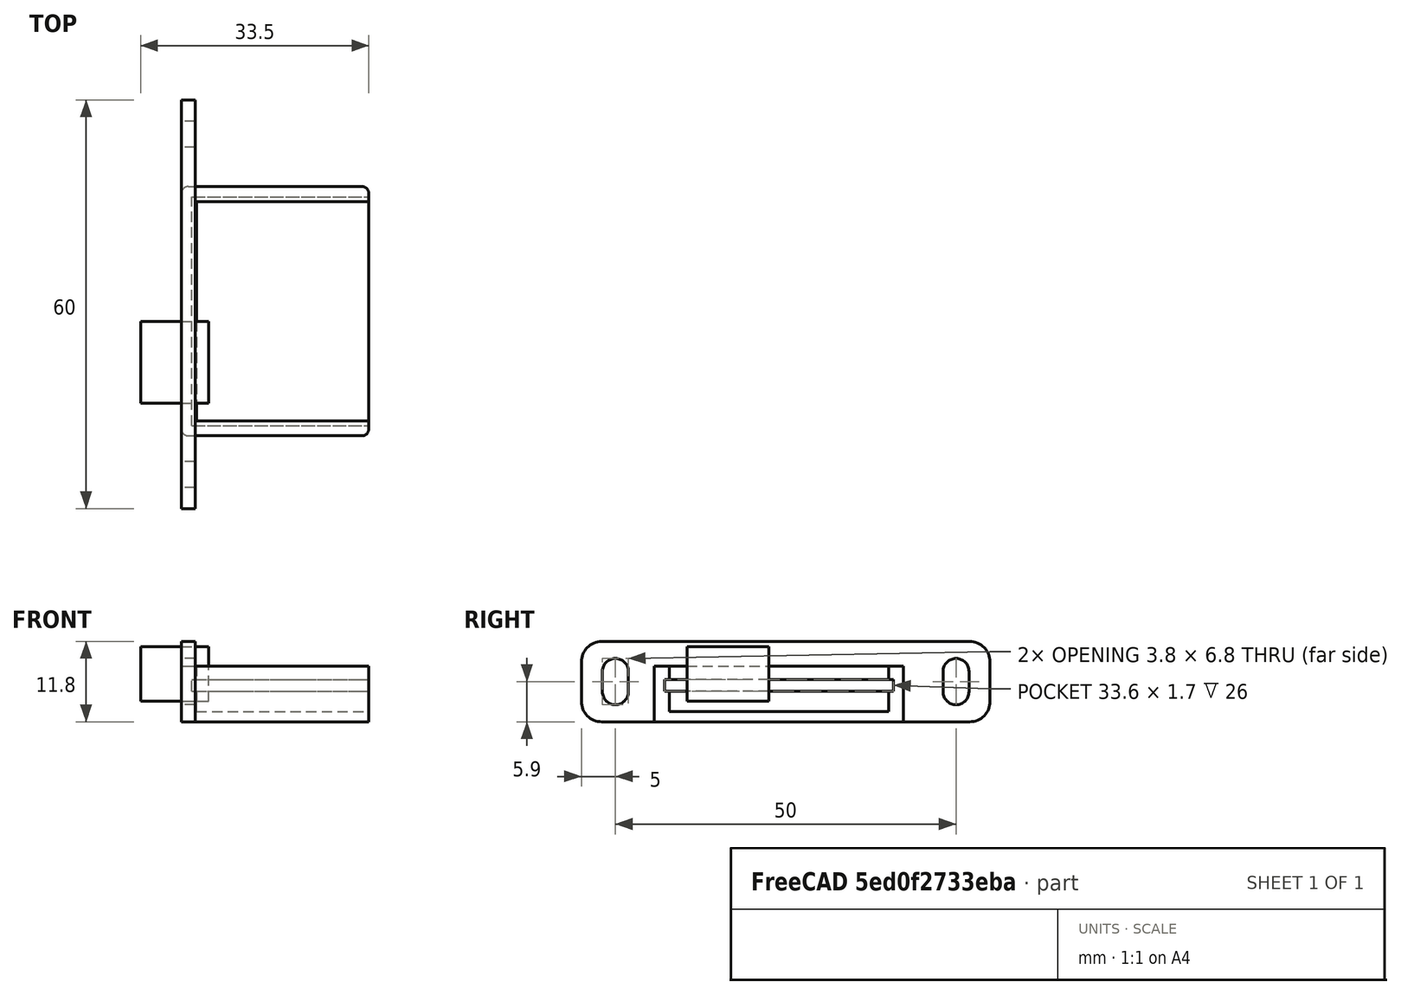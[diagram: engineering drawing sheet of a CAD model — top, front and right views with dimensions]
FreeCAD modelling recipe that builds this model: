
FCSTD DOCUMENT  (FreeCAD 0.19R)
Label: lion_manager
License: All rights reserved
LicenseURL: http://en.wikipedia.org/wiki/All_rights_reserved
objects: Part::Box×4, App::Part×3, Part::Feature×3, Part::MultiFuse×2, Part::Cut×2, Part::Fillet×1, Spreadsheet::Sheet×1
note: 12 computed .brp shape members not serialized (recipe doc carries the construction recipe); baked Part::Feature solids carry a one-line shape summary decoded from their .brp

FEATURE [Part::Box] Box025  label="external cube001"
  AttacherType = Attacher::AttachEngine3D
  Height = 8.2
  Length = 27.5
  Width = 36.6
  expr: Height = <<p_usb>>.bottom_wall + <<p_usb>>.pcb_under + <<p_usb>>.pcb_z + <<p_usb>>.pcb_above
  expr: Width = <<p_usb>>.pcb_y + 2 * <<p_usb>>.side_wall
  expr: Length = <<p_usb>>.pcb_x + <<p_usb>>.side_wall
FEATURE [Part::Fillet] Fillet001  label="external fillet001"
  Base = -> Box025
  Edges = 4 edges r=1: [Edge1,Edge3,Edge5,Edge7]
FEATURE [Part::Box] Box026  label="internal cube001"
  AttacherType = Attacher::AttachEngine3D
  Height = 6.7
  Length = 26.1
  Placement = pos=(2.2,2.2,1.5) rot=(0,0,1;0rad)
  Width = 32.2
  expr: .Placement.Base.y = <<p_usb>>.side_wall + <<p_usb>>.pcb_side_lane
  expr: .Placement.Base.x = <<p_usb>>.side_wall + <<p_usb>>.pcb_side_lane
  expr: .Placement.Base.z = <<p_usb>>.bottom_wall
  expr: Height = <<p_usb>>.pcb_under + <<p_usb>>.pcb_z + <<p_usb>>.pcb_above
  expr: Width = <<p_usb>>.pcb_y - 2 * <<p_usb>>.pcb_side_lane
  expr: Length = <<p_usb>>.pcb_x - 2 * <<p_usb>>.pcb_side_lane + <<p_usb>>.side_wall
FEATURE [Part::Box] Box027  label="pcb extract cube001"
  AttacherType = Attacher::AttachEngine3D
  Height = 1.7
  Length = 26
  Placement = pos=(1.5,1.5,4.5) rot=(0,0,1;0rad)
  Width = 33.6
  expr: .Placement.Base.y = <<p_usb>>.side_wall
  expr: .Placement.Base.x = <<p_usb>>.side_wall
  expr: Length = <<p_usb>>.pcb_x
  expr: Width = <<p_usb>>.pcb_y
  expr: .Placement.Base.z = <<p_usb>>.bottom_wall + <<p_usb>>.pcb_under
  expr: Height = <<p_usb>>.pcb_z
FEATURE [Part::MultiFuse] Fusion003  label="extract fusion001"
  Shapes = -> [Box026,Box027]
FEATURE [Spreadsheet::Sheet] Spreadsheet  label="p_usb"
  cells = A1=pcb_x; B1(pcb_x)=26; A2=pcb_y; B2(pcb_y)=33.6; A3=pcb_z; B3(pcb_z)=1.7; A4=pcb_under; B4(pcb_under)=3; A5=side_wall; B5(side_wall)=1.5; A6=pcb_side_lane; B6(pcb_side_lane)=0.7; A7=bottom_wall; B7(bottom_wall)=1.5; A8=pcb_above; B8(pcb_above)=2
FEATURE [Part::Cut] Cut002  label="lion manager cut"
  Base = -> Fillet001
  Placement = pos=(-26,-1,-1) rot=(0,0,1;0rad)
  Tool = -> Fusion003
FEATURE [App::Part] Part014  label="lion manager mockup part"
  Group = -> [Cut002]
  Origin = -> Origin021
  Placement = pos=(10,36,28) rot=(0.57735,0.57735,0.57735;4.18879rad)
FEATURE [Part::Box] Box024  label="lion micro usb hole"
  AttacherType = Attacher::AttachEngine3D
  Height = 8
  Length = 12
  Placement = pos=(-32,15.8,2) rot=(0,0,-1;1.5708rad)
  Width = 10
FEATURE [App::Part] Part015  label="lion manager mockup hole part"
  Group = -> [Box024]
  Origin = -> Origin022
  Placement = pos=(10,36,27) rot=(0.57735,0.57735,0.57735;4.18879rad)
FEATURE [Part::Feature] Part014001  label="lion manager mockup part001"
  shape: bbox 27.5 x 36.6 x 8.2 mm, 22 faces (baked)
FEATURE [Part::Feature] Body001001  label="attach plane y rotated dir001"
  Placement = pos=(-24,-11.7,-1) rot=(0,-1,0;1.5708rad)
  shape: bbox 2 x 60 x 11.8 mm, 20 faces (baked)
FEATURE [Part::MultiFuse] Fusion  label="body fusion"
  Shapes = -> [Body001001,Part014001]
FEATURE [Part::Feature] Part015001  label="lion manager mockup hole"
  shape: bbox 10 x 12 x 8 mm, 6 faces (baked)
FEATURE [Part::Cut] Cut  label="body cut"
  Base = -> Fusion
  Tool = -> Part015001
FEATURE [App::Part] Part015002  label="lion manager mockup part002"
  Group = -> [Cut]
  Origin = -> Origin023
  Placement = pos=(10,36,28) rot=(0.57735,0.57735,0.57735;4.18879rad)
